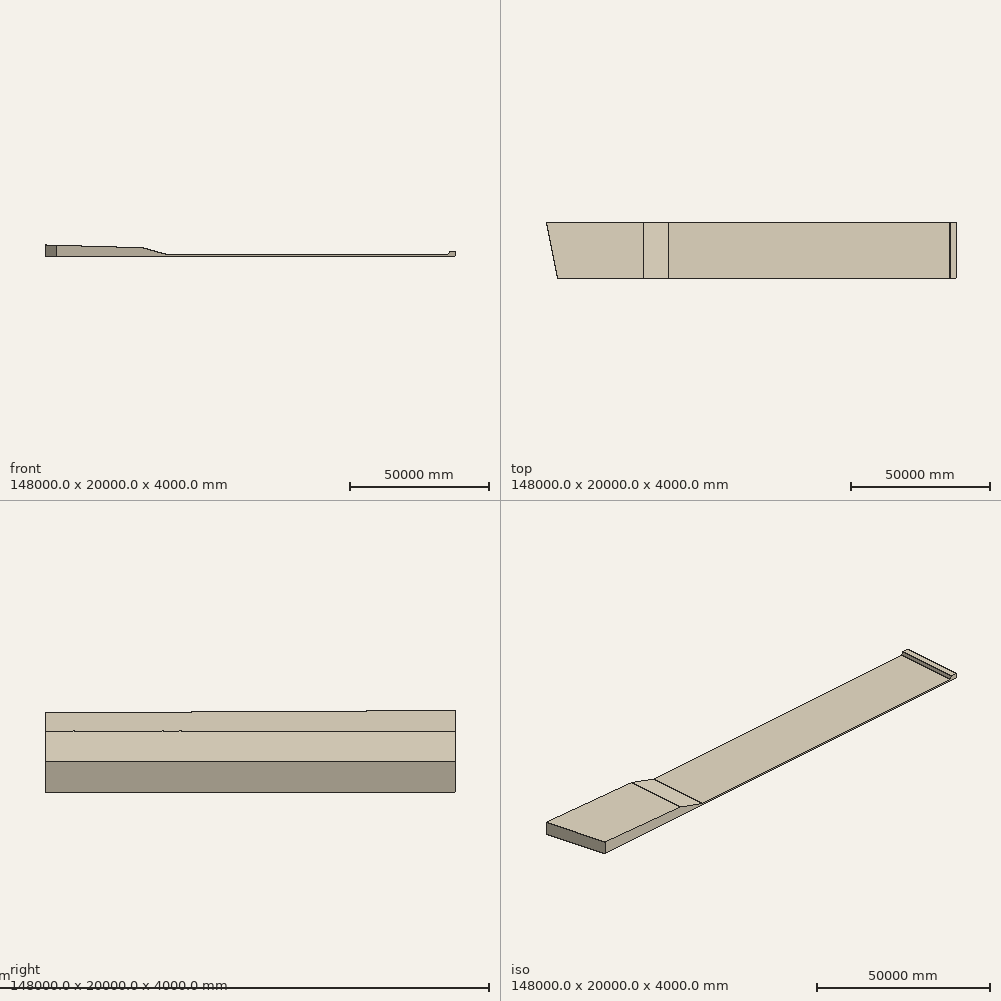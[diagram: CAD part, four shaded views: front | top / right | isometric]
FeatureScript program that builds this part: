
annotation { "Feature Type Name" : "Feature", "Feature Type Description" : "" }
export const myFeature = defineFeature(function(context is Context, id is Id, definition is map)
    precondition{}
    {
        {
            var Q0;
            Q0=qCreatedBy(makeId("Front.planeOp"),FACE);
            var sketch = newSketch(context, id + "F0", { "sketchPlane" : qUnion([Q0])});
            skLineSegment(sketch, "E0", {"start": v(-59684.28, 0) * mm, "end": v(88315.72, 0) * mm});
            skLineSegment(sketch, "E1", {"start": v(-59684.28, 0) * mm, "end": v(-59684.28, 4000) * mm});
            skLineSegment(sketch, "E2", {"start": v(-59684.28, 4000) * mm, "end": v(-24684.28, 3000) * mm});
            skLineSegment(sketch, "E3", {"start": v(-24684.28, 3000) * mm, "end": v(-15684.28, 500) * mm});
            skLineSegment(sketch, "E4", {"start": v(-15684.28, 500) * mm, "end": v(85815.72, 500) * mm});
            skLineSegment(sketch, "E5", {"start": v(85815.72, 500) * mm, "end": v(86315.72, 1500) * mm});
            skLineSegment(sketch, "E6", {"start": v(86315.72, 1500) * mm, "end": v(88315.72, 1500) * mm});
            skLineSegment(sketch, "E7", {"start": v(88315.72, 0) * mm, "end": v(88315.72, 1500) * mm});
            skSolve(sketch);
        }
        {
            var Q0;
            Q0 = qSketchRegion(id + "F0", true);
            extrude(context, id + "F1", {"entities" : qUnion([Q0]), "endBound" : BoundingType.SYMMETRIC, "depth" : 20000 * mm});
        }
        {
            var Q0;
            Q0=makeQuery(id+"F1.opExtrude","SWEPT_FACE",FACE,{"disambiguationData":[OSD([sQuery(id+"F0.wireOp",EDGE,"E0")])]});
            var sketch = newSketch(context, id + "F2", { "sketchPlane" : qUnion([Q0])});
            skLineSegment(sketch, "E8", {"start": v(-59684.28, -10000) * mm, "end": v(-55684.28, 10000) * mm});
            skLineSegment(sketch, "E9", {"start": v(-55684.28, 10000) * mm, "end": v(-59684.28, 10000) * mm});
            skLineSegment(sketch, "E10", {"start": v(-59684.28, 10000) * mm, "end": v(-59684.28, -10000) * mm});
            skSolve(sketch);
        }
        {
            var Q0;
            Q0 = qSketchRegion(id + "F2", true);
            extrude(context, id + "F3", {"entities" : qUnion([Q0]), "operationType" : NewBodyOperationType.REMOVE, "endBound" : BoundingType.THROUGH_ALL, "oppositeDirection" : true, "depth" : 14989.11 * mm});
        }
    });
